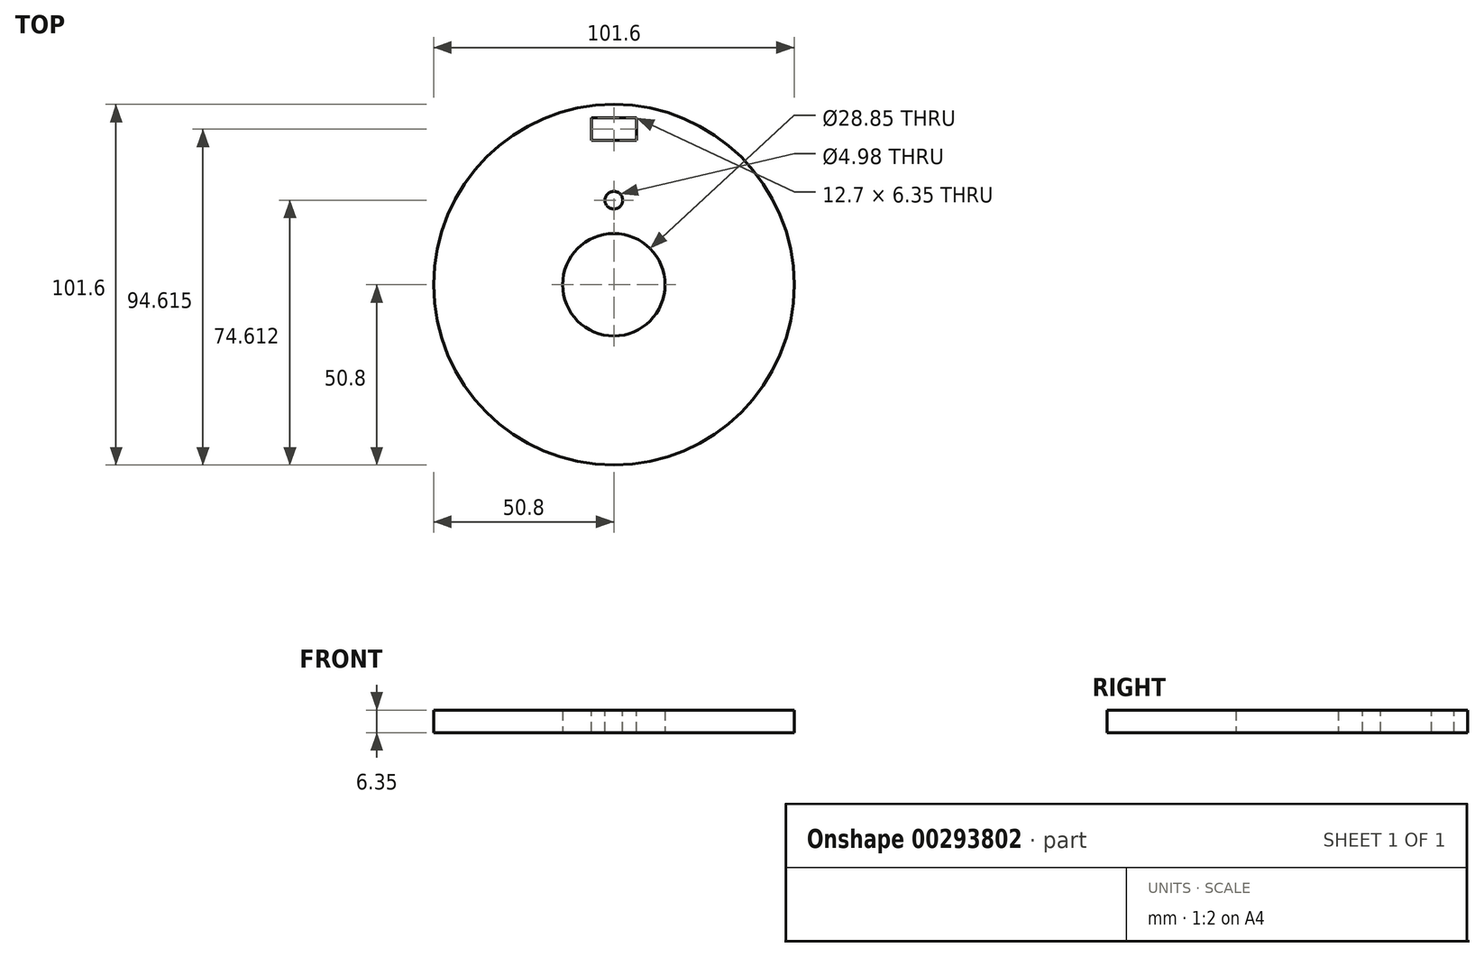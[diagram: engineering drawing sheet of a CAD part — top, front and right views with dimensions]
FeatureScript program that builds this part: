
annotation { "Feature Type Name" : "Feature", "Feature Type Description" : "" }
export const myFeature = defineFeature(function(context is Context, id is Id, definition is map)
    precondition{}
    {
        {
            var Q0;
            Q0=qCreatedBy(makeId("Top.planeOp"),FACE);
            var sketch = newSketch(context, id + "F0", { "sketchPlane" : qUnion([Q0])});
            skCircle(sketch, "E0", {"center": v(0, 0) * mm, "radius": 50.8 * mm});
            skCircle(sketch, "E1", {"center": v(0, 0) * mm, "radius": 14.43 * mm});
            skSolve(sketch);
        }
        {
            var Q0;
            Q0=makeQuery(id+"F0.imprint","IMPRINT",FACE,{"disambiguationData":[TD([[makeQuery(id+"F0.imprint","IMPRINT",EDGE,{"derivedFrom":sQuery(id+"F0.wireOp",EDGE,"E0")}),1.0]])]});
            var Q1;
            Q1=qSketchRegion(id+"F0",true);
            extrude(context, id + "F1", {"entities" : qUnion([Q0, Q1]), "depth" : 6.35 * mm});
        }
        {
            var Q0;
            Q0=makeQuery(id+"F1.opExtrude","CAP_FACE",FACE,{"disambiguationData":[OSD([sQuery(id+"F0.wireOp",EDGE,"E0"),sQuery(id+"F0.wireOp",EDGE,"E1")])],"isStart":false});
            var sketch = newSketch(context, id + "F2", { "sketchPlane" : qUnion([Q0])});
            skLineSegment(sketch, "E2.bottom", {"start": v(-6.35, 47) * mm, "end": v(6.35, 47) * mm});
            skLineSegment(sketch, "E2.top", {"start": v(-6.35, 40.64) * mm, "end": v(6.35, 40.64) * mm});
            skLineSegment(sketch, "E2.left", {"start": v(-6.35, 47) * mm, "end": v(-6.35, 40.64) * mm});
            skLineSegment(sketch, "E2.right", {"start": v(6.35, 47) * mm, "end": v(6.35, 40.64) * mm});
            skCircle(sketch, "E3", {"center": v(0, 0) * mm, "radius": 50.8 * mm, "construction": true});
            skPoint(sketch, "E4.middle", {"position": v(0, 40.38) * mm});
            skSolve(sketch);
        }
        {
            var Q0;
            Q0=qSketchRegion(id+"F2",true);
            extrude(context, id + "F3", {"entities" : qUnion([Q0]), "operationType" : NewBodyOperationType.REMOVE, "endBound" : BoundingType.THROUGH_ALL, "oppositeDirection" : true, "depth" : 25.4 * mm});
        }
        {
            var Q0;
            Q0=makeQuery(id+"F1.opExtrude","CAP_FACE",FACE,{"disambiguationData":[OSD([sQuery(id+"F0.wireOp",EDGE,"E0"),sQuery(id+"F0.wireOp",EDGE,"E1")])],"isStart":false});
            var sketch = newSketch(context, id + "F4", { "sketchPlane" : qUnion([Q0])});
            skCircle(sketch, "E5", {"center": v(0, 23.81) * mm, "radius": 2.49 * mm});
            skSolve(sketch);
        }
        {
            var Q0;
            Q0 = qSketchRegion(id + "F4", true);
            extrude(context, id + "F5", {"entities" : qUnion([Q0]), "operationType" : NewBodyOperationType.REMOVE, "endBound" : BoundingType.THROUGH_ALL, "oppositeDirection" : true, "depth" : 25.4 * mm});
        }
    });
